# Revit family: Hager-Volta-IP30-Flush_mounted-sistema-NoHosted-ES-es
name_source: partatom
category: Electrical Equipment
units: mm (PartAtom-declared; Revit-internal decimal feet)

## family parameters
Always vertical = Yes
Cut with Voids When Loaded = No
Panel Configuration = Two Columns, Circuits Across
Part Type = Panelboard
Room Calculation Point = No
Round Connector Dimension = Use Diameter
Shared = No
Work Plane-Based = Yes

## types (12) — shared parameters
Default Elevation = 1219 mm
EF000003 - Tipo de montaje = EV000383 - Montado empotrado (escayola)
EF000007 - Color = EV000202 - Blanco
EF000008 - Anchura = 348 mm  [stored 1.14173 ft]
EF000049 - Profundidad = 94 mm  [stored 0.308399 ft]
EF000116 - Número RAL = 9010
EF000118 - Con placa de montaje = No
EF000218 - Profundidad de instalación = 90 mm  [stored 0.295276 ft]
EF000339 - Tipo de cubierta = EV004216 - Puerta
EF000846 - Anchura de instalación = 335 mm  [stored 1.09908 ft]
EF001062 - Versión de EMC = No
EF001088 - Posibilidad de extensión = Yes
EF001131 - Profundidad interna = 92 mm
EF001134 - Carril DIN = Yes
EF002950 - Anchura de unidades de división = 12
EF004462 - Tipo de cierre = EV000154 - Otros
EF005474 - Grado de protección (IP) = EV006410 - IP30
EF006306 - Con cierre = No
EF009212 - Versión de la cubierta = EV009916 - Con muesca
EF015777 - Borne neutro = No
EF015941 - Puerta de transmisión de señal = No
HG000001 - Número de columnas = 1
HG000002 - Con puerta o tapa = Yes
HG000003 - Gama = Volta
HG000005 - Grosor = 3 mm  [stored 0.00984252 ft]
HG000006 - Empotrado = Yes
HG000009 - Puerta batiente doble = No
HG000010 - Puertas asimétricas = No
HG000011 - Filas vacías desde abajo = No
HG000017 - Distancia entre polos = 18 mm  [stored 0.0590551 ft]
Manufacturer = Hager
Type Comments = Volta
zero-valued in all types: HG000007 - Número de columnas vacías, HG000008 - Número de filas vacías

## per-type parameters (varying)
| type | EF000040 - Altura | EF000266 - Número de filas | EF000332 - Altura de la instalación | EF001596 - Material de la carcasa | EF006244 - Tapa/puerta transparente | EF015776 - Borne de tierra | HG000004 - Referencia del fabricante | Model |
| Montado empotrado IP30 A348 A356 P94.5 12 unidad de división - VU12EP | 356 mm | 1 | 321 mm | EV000139 - Plástico | No | Yes | VU12EP | VU12EP |
| Montado empotrado IP30 A348 A356 P94.5 12 unidad de división - VU12ET | 356 mm | 1 | 321 mm | EV000139 - Plástico | Yes | Yes | VU12ET | VU12ET |
| Montado empotrado IP30 A348 A505.5 P94.5 12 unidad de división - VU24EP | 506 mm | 2 | 471 mm | EV000139 - Plástico | No | Yes | VU24EP | VU24EP |
| Montado empotrado IP30 A348 A505.5 P94.5 12 unidad de división - VU24ET | 506 mm | 2 | 471 mm | EV000139 - Plástico | Yes | Yes | VU24ET | VU24ET |
| Montado empotrado IP30 A348 A630.5 P94.5 12 unidad de división - VU36EP | 630 mm | 3 | 596 mm | EV000139 - Plástico | No | Yes | VU36EP | VU36EP |
| Montado empotrado IP30 A348 A630.5 P94.5 12 unidad de división - VU36ET | 630 mm | 3 | 596 mm | EV000139 - Plástico | Yes | Yes | VU36ET | VU36ET |
| Montado empotrado IP30 A348 A630.5 P94.5 12 unidad de división - VU36NCT | 630 mm | 3 | 596 mm | EV000139 - Plástico | No | No | VU36NCT | VU36NCT |
| Montado empotrado IP30 A348 A755.5 P94.5 12 unidad de división - VU48EP | 756 mm | 4 | 721 mm | EV000139 - Plástico | No | Yes | VU48EP | VU48EP |
| Montado empotrado IP30 A348 A755.5 P94.5 12 unidad de división - VU48ET | 756 mm | 4 | 721 mm | EV000139 - Plástico | Yes | Yes | VU48ET | VU48ET |
| Montado empotrado IP30 A348 A755.5 P94.5 12 unidad de división - VU48NCT | 756 mm | 4 | 721 mm | EV000139 - Plástico | No | No | VU48NCT | VU48NCT |
| Montado empotrado IP30 A348 A880.5 P94.5 12 unidad de división - VU60EP | 880 mm  [stored 2.88714 ft] | 5 | 846 mm  [stored 2.77559 ft] | EV000154 - Otros | No | Yes | VU60EP | VU60EP |
| Montado empotrado IP30 A348 A880.5 P94.5 12 unidad de división - VU60ET | 880 mm  [stored 2.88714 ft] | 5 | 846 mm  [stored 2.77559 ft] | EV000154 - Otros | Yes | Yes | VU60ET | VU60ET |

note: [stored X ft] marks values corroborated as IEEE doubles in the binary element streams (Revit-internal decimal feet)

## geometry (parser evidence)
native form markers: Sweep x13
no freeform markers — native parametric forms only
